# Revit family: LTV767SP6L3KUVNB
name_source: partatom
category: Lighting Fixtures
units: mm (PartAtom-declared; Revit-internal decimal feet)

## family parameters
Cut with Voids When Loaded = No
Host = Face
Light Source = Yes
Part Type = Normal
Room Calculation Point = No
Round Connector Dimension = Use Diameter
Shared = No

## types (1)
- LTV767SP/6L3KUV/NB
    Apparent Load = 11 VA
    Assembly Code = D5020200
    Color Filter = 16777215
    Composite Housing material = Plastic-Fiberglass
    Default Elevation = 0 "
    Description = Minivault incorporates more than 50 years of in-grade experience into every luminaire. A commitment to produce the most durable product possible is the core of the series, which now includes new low wattage pulse start metal halide lamps and LEDs expanding into residential applications.
    Diameter = 6 "
    Dimming Lamp Color Temperature Shift = <None>
    Emit Shape Visible in Rendering = No
    Emit from Circle Diameter = 5 "
    Finish = Cast Bronze, Natural Finish
    Frequency = 60 Hz
    Full Load Current = 11 A
    Glass Material = Glass-Clear
    LED = Default Light Source
    Lamp = LED
    Lens Ring Material = Metal-Bronze
    Manufacturer = KIM Lighting
    Model = LTV767SP/6L3KUV/NB
    Note Text = LF
    Note Visible = Yes
    Number of Poles = 1
    OmniClass Number = 23-80 70 14 11 21
    OmniClass Title = Buried Uplights
    Photometric Web File = ltv767sp-6led.ies
    Power Factor = 1
    Series = In-grade/ Landscape
    Specification = Energy efficient LED models
Brass or aluminum housing for durability
Hex cell louver and prismatic spread lens options
    Tilt Angle = -90.00°
    Type Comments = Lighting Fixture
    URL = https://www.currentlighting.com
    Voltage = 120 to 277V
    Wattage Comments = 11W
    White Surface = Paint  - White Texture

## geometry (parser evidence)
native form markers: Sweep x2
no freeform markers — native parametric forms only
